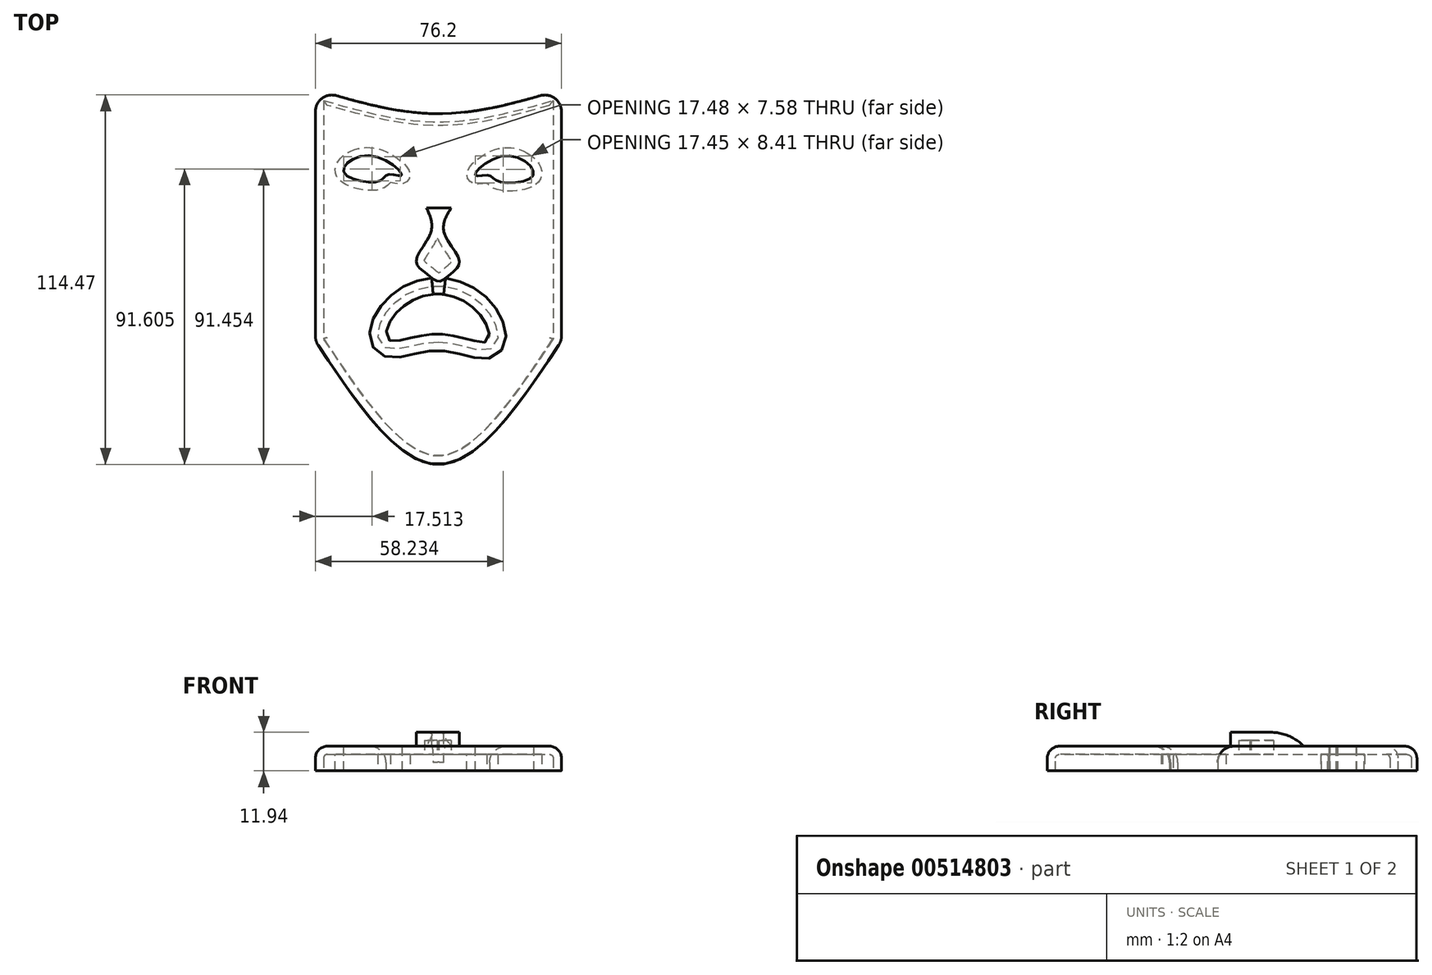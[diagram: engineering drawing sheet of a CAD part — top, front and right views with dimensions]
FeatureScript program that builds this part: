
annotation { "Feature Type Name" : "Feature", "Feature Type Description" : "" }
export const myFeature = defineFeature(function(context is Context, id is Id, definition is map)
    precondition{}
    {
        {
            var Q0;
            Q0=qCreatedBy(makeId("Top.planeOp"),FACE);
            var sketch = newSketch(context, id + "F0", { "sketchPlane" : qUnion([Q0])});
            skLineSegment(sketch, "E0", {"start": v(38.1, 44.28) * mm, "end": v(38.1, -33.7) * mm});
            skLineSegment(sketch, "E1", {"start": v(-38.1, 44.28) * mm, "end": v(-38.1, -33.7) * mm});
            skFitSpline(sketch, "E2", {"points": [v(-38.1, -33.7) * mm, v(0, -71.9) * mm, v(38.1, -33.7) * mm], "startDerivative": vector(76.2, -114.57) * mm, "endDerivative": vector(76.2, 114.57) * mm});
            skFitSpline(sketch, "E3", {"points": [v(-38.1, 44.28) * mm, v(0, 36.78) * mm, v(38.1, 44.28) * mm], "startDerivative": vector(76.2, -22.5) * mm, "endDerivative": vector(76.2, 22.5) * mm});
            skFitSpline(sketch, "E4", {"points": [v(-29.33, 18.75) * mm, v(-21, 23.76) * mm, v(-11.4, 17.72) * mm, v(-15.58, 17.92) * mm, v(-18.5, 15.84) * mm, v(-29.33, 18.75) * mm]});
            skPoint(sketch, "E5", {"position": v(-21, 39.57) * mm});
            skPoint(sketch, "E6", {"position": v(21, 39.57) * mm});
            skPoint(sketch, "E7", {"position": v(-38.1, 18.75) * mm});
            skPoint(sketch, "E8", {"position": v(-18.5, -60.58) * mm});
            skPoint(sketch, "E9", {"position": v(-15.58, -63.62) * mm});
            skPoint(sketch, "E10", {"position": v(15.58, -63.62) * mm});
            skPoint(sketch, "E11", {"position": v(18.5, -60.58) * mm});
            skPoint(sketch, "E12", {"position": v(38.1, 18.75) * mm});
            skPoint(sketch, "E13", {"position": v(-11.4, 37.69) * mm});
            skPoint(sketch, "E14", {"position": v(11.4, 37.69) * mm});
            skPoint(sketch, "E15", {"position": v(-29.33, 41.73) * mm});
            skPoint(sketch, "E16", {"position": v(29.33, 41.73) * mm});
            skFitSpline(sketch, "E17", {"points": [v(11.4, 17.72) * mm, v(21, 23.76) * mm, v(29.33, 17.72) * mm, v(18.5, 15.84) * mm, v(15.58, 17.72) * mm, v(11.4, 17.72) * mm]});
            skFitSpline(sketch, "E18", {"points": [v(0, -19.09) * mm, v(13.44, -26.2) * mm, v(15.27, -33.7) * mm, v(0, -31.48) * mm, v(-15.58, -33.3) * mm, v(-13.77, -25.8) * mm, v(0, -19.09) * mm]});
            skSolve(sketch);
        }
        {
            var Q0;
            Q0=makeQuery(id+"F0.imprint","IMPRINT",FACE,{"disambiguationData":[TD([[makeQuery(id+"F0.imprint","IMPRINT",EDGE,{"derivedFrom":sQuery(id+"F0.wireOp",EDGE,"E0")}),-1.0]])]});
            var Q1;
            {var subQ1=sQuery(id+"F0.wireOp",EDGE,"E1");Q1=makeQuery(id+"F0.imprint","IMPRINT",FACE,{"disambiguationData":[TD([[makeQuery(id+"F0.imprint","IMPRINT",EDGE,{"derivedFrom":subQ1}),1.0]])]});}
            extrude(context, id + "F1", {"entities" : qUnion([Q0, Q1]), "depth" : 7.62 * mm});
        }
        {
            var Q0;
            Q0=qCreatedBy(makeId("Top.planeOp"),FACE);
            var sketch = newSketch(context, id + "F2", { "sketchPlane" : qUnion([Q0])});
            skPoint(sketch, "E19", {"position": v(0, 7.57) * mm});
            skPoint(sketch, "E20", {"position": v(3.91, 7.57) * mm});
            skPoint(sketch, "E21", {"position": v(-3.66, 7.57) * mm});
            skPoint(sketch, "E22", {"position": v(-2.36, 0) * mm});
            skPoint(sketch, "E23", {"position": v(1.75, 0) * mm});
            skPoint(sketch, "E24", {"position": v(0, -15.14) * mm});
            skPoint(sketch, "E25", {"position": v(3.91, -12.76) * mm});
            skPoint(sketch, "E26", {"position": v(-3.66, -12.76) * mm});
            skPoint(sketch, "E27", {"position": v(-6.9, -8.87) * mm});
            skPoint(sketch, "E28", {"position": v(6.5, -8.87) * mm});
            skFitSpline(sketch, "E29", {"points": [v(-3.66, 7.57) * mm, v(-2.36, 0) * mm, v(-6.9, -8.87) * mm, v(-3.66, -12.76) * mm, v(0, -15.14) * mm, v(3.91, -12.76) * mm, v(6.5, -8.87) * mm, v(1.75, 0) * mm, v(3.91, 7.57) * mm], "startDerivative": vector(24.14, -53.97) * mm, "endDerivative": vector(31.94, 53.32) * mm});
            skLineSegment(sketch, "E30", {"start": v(-3.66, 7.57) * mm, "end": v(3.91, 7.57) * mm});
            skSolve(sketch);
        }
        {
            var Q0;
            Q0=qSketchRegion(id+"F2",true);
            extrude(context, id + "F3", {"entities" : qUnion([Q0]), "operationType" : NewBodyOperationType.ADD, "depth" : 11.94 * mm});
        }
        {
            var Q0;
            Q0=makeQuery(id+"F1.opExtrude","CAP_EDGE",EDGE,{"disambiguationData":[OSD([sQuery(id+"F0.wireOp",EDGE,"E0")])],"isStart":false});
            var Q1;
            Q1=makeQuery(id+"F1.opExtrude","CAP_EDGE",EDGE,{"disambiguationData":[OSD([sQuery(id+"F0.wireOp",EDGE,"E2")])],"isStart":false});
            var Q2;
            Q2=makeQuery(id+"F1.opExtrude","CAP_EDGE",EDGE,{"disambiguationData":[OSD([sQuery(id+"F0.wireOp",EDGE,"E1")])],"isStart":false});
            var Q3;
            Q3=makeQuery(id+"F1.opExtrude","CAP_EDGE",EDGE,{"disambiguationData":[OSD([sQuery(id+"F0.wireOp",EDGE,"E3")])],"isStart":false});
            fillet(context, id + "F4", {"entities" : qUnion([Q0, Q1, Q2, Q3]), "radius" : 3.68 * mm, "tangentPropagation" : true, "allowEdgeOverflow" : false});
        }
        {
            var Q0;
            Q0=makeQuery(id+"F1.opExtrude","CAP_FACE",FACE,{"disambiguationData":[OSD([sQuery(id+"F0.wireOp",EDGE,"E0"),sQuery(id+"F0.wireOp",EDGE,"E1"),sQuery(id+"F0.wireOp",EDGE,"E2"),sQuery(id+"F0.wireOp",EDGE,"E3"),sQuery(id+"F0.wireOp",EDGE,"E4"),sQuery(id+"F0.wireOp",EDGE,"E17"),sQuery(id+"F0.wireOp",EDGE,"a7bd3cff-36a1-48b1-a12a-04305ffe60e2")])],"isStart":true});
            shell(context, id + "F5", {"entities" : qUnion([Q0]), "thickness" : 2.54 * mm});
        }
        {
            var Q0;
            Q0=makeQuery(id+"F4.opFillet","BLEND_EDGE",EDGE,{"blendedFrom":[makeQuery(id+"F1.opExtrude","CAP_EDGE",EDGE,{"disambiguationData":[OSD([sQuery(id+"F0.wireOp",EDGE,"E0")])],"isStart":false}),makeQuery(id+"F1.opExtrude","CAP_EDGE",EDGE,{"disambiguationData":[OSD([sQuery(id+"F0.wireOp",EDGE,"E3")])],"isStart":false})],"blendedInto":[]});
            var Q1;
            Q1=makeQuery(id+"F4.opFillet","BLEND_EDGE",EDGE,{"blendedFrom":[makeQuery(id+"F1.opExtrude","CAP_EDGE",EDGE,{"disambiguationData":[OSD([sQuery(id+"F0.wireOp",EDGE,"E1")])],"isStart":false}),makeQuery(id+"F1.opExtrude","CAP_EDGE",EDGE,{"disambiguationData":[OSD([sQuery(id+"F0.wireOp",EDGE,"E3")])],"isStart":false})],"blendedInto":[]});
            var Q2;
            Q2=makeQuery(id+"F4.opFillet","BLEND_EDGE",EDGE,{"blendedFrom":[makeQuery(id+"F1.opExtrude","CAP_EDGE",EDGE,{"disambiguationData":[OSD([sQuery(id+"F0.wireOp",EDGE,"E0")])],"isStart":false}),makeQuery(id+"F1.opExtrude","CAP_EDGE",EDGE,{"disambiguationData":[OSD([sQuery(id+"F0.wireOp",EDGE,"E2")])],"isStart":false})],"blendedInto":[]});
            var Q3;
            Q3=makeQuery(id+"F4.opFillet","BLEND_EDGE",EDGE,{"blendedFrom":[makeQuery(id+"F1.opExtrude","CAP_EDGE",EDGE,{"disambiguationData":[OSD([sQuery(id+"F0.wireOp",EDGE,"E1")])],"isStart":false}),makeQuery(id+"F1.opExtrude","CAP_EDGE",EDGE,{"disambiguationData":[OSD([sQuery(id+"F0.wireOp",EDGE,"E2")])],"isStart":false})],"blendedInto":[]});
            fillet(context, id + "F6", {"entities" : qUnion([Q0, Q1, Q2, Q3]), "radius" : 5.08 * mm, "tangentPropagation" : true, "allowEdgeOverflow" : false});
        }
        {
            var Q0;
            Q0=makeQuery(id+"F3.opExtrude","CAP_EDGE",EDGE,{"disambiguationData":[OSD([sQuery(id+"F2.wireOp",EDGE,"E30")])],"isStart":false});
            fillet(context, id + "F7", {"entities" : qUnion([Q0]), "radius" : 14.1 * mm, "tangentPropagation" : true, "allowEdgeOverflow" : false});
        }
        {
            var Q0;
            Q0=makeQuery(id+"F1.opExtrude","CAP_EDGE",EDGE,{"disambiguationData":[OSD([sQuery(id+"F0.wireOp",EDGE,"E18")])],"isStart":false});
            fillet(context, id + "F8", {"entities" : qUnion([Q0]), "radius" : 5.08 * mm, "tangentPropagation" : true, "allowEdgeOverflow" : false});
        }
    });
